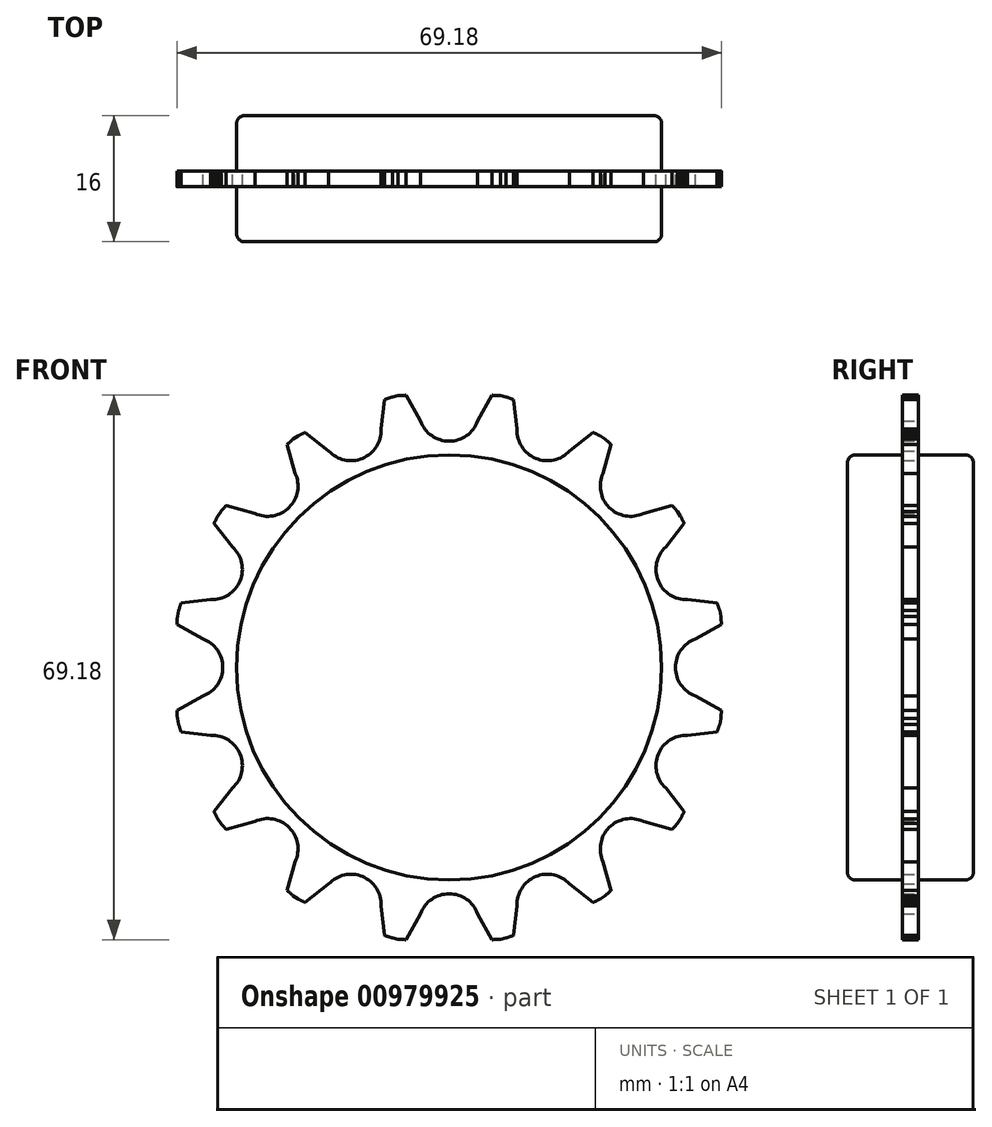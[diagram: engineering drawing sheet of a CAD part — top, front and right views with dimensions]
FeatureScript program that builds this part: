
annotation { "Feature Type Name" : "Feature", "Feature Type Description" : "" }
export const myFeature = defineFeature(function(context is Context, id is Id, definition is map)
    precondition{}
    {
        {
            var Q0;
            Q0=qCreatedBy(makeId("Front.planeOp"),FACE);
            var sketch = newSketch(context, id + "F0", { "sketchPlane" : qUnion([Q0])});
            skArc(sketch, "E0", {"start": v(-3.62, 31.28) * mm, "mid": v(0, 28.75) * mm, "end": v(3.62, 31.28) * mm});
            skPoint(sketch, "E1.center", {"position": v(0, -0.09) * mm});
            skArc(sketch, "E2.trimOffspring", {"start": v(6.5, 34.52) * mm, "mid": v(5.98, 34.55) * mm, "end": v(5.47, 34.59) * mm});
            skArc(sketch, "E3.1.5", {"start": v(-5.47, 34.59) * mm, "mid": v(-5.98, 34.55) * mm, "end": v(-6.5, 34.52) * mm});
            skLineSegment(sketch, "E4", {"start": v(3.62, 31.28) * mm, "end": v(5.47, 34.59) * mm});
            skLineSegment(sketch, "E5.MirrorCS", {"start": v(-3.62, 31.28) * mm, "end": v(-5.47, 34.59) * mm});
            skArc(sketch, "E6.1.0", {"start": v(-15.31, 27.51) * mm, "mid": v(-11, 26.56) * mm, "end": v(-8.63, 30.28) * mm});
            skLineSegment(sketch, "E6.1.1", {"start": v(-8.63, 30.28) * mm, "end": v(-8.18, 34.05) * mm});
            skArc(sketch, "E6.1.2", {"start": v(-7.21, 34.37) * mm, "mid": v(-7.7, 34.21) * mm, "end": v(-8.18, 34.05) * mm});
            skArc(sketch, "E6.1.3", {"start": v(-18.3, 29.86) * mm, "mid": v(-18.75, 29.63) * mm, "end": v(-19.2, 29.4) * mm});
            skLineSegment(sketch, "E6.1.4", {"start": v(-15.31, 27.51) * mm, "end": v(-18.3, 29.86) * mm});
            skArc(sketch, "E6.2.0", {"start": v(-24.67, 19.56) * mm, "mid": v(-20.33, 20.33) * mm, "end": v(-19.56, 24.67) * mm});
            skLineSegment(sketch, "E6.2.1", {"start": v(-19.56, 24.67) * mm, "end": v(-20.59, 28.33) * mm});
            skArc(sketch, "E6.2.2", {"start": v(-19.82, 29) * mm, "mid": v(-20.2, 28.66) * mm, "end": v(-20.59, 28.33) * mm});
            skArc(sketch, "E6.2.3", {"start": v(-28.33, 20.59) * mm, "mid": v(-28.66, 20.2) * mm, "end": v(-29, 19.82) * mm});
            skLineSegment(sketch, "E6.2.4", {"start": v(-24.67, 19.56) * mm, "end": v(-28.33, 20.59) * mm});
            skArc(sketch, "E6.3.0", {"start": v(-30.28, 8.63) * mm, "mid": v(-26.56, 11) * mm, "end": v(-27.51, 15.31) * mm});
            skLineSegment(sketch, "E6.3.1", {"start": v(-27.51, 15.31) * mm, "end": v(-29.86, 18.3) * mm});
            skArc(sketch, "E6.3.2", {"start": v(-29.4, 19.2) * mm, "mid": v(-29.63, 18.75) * mm, "end": v(-29.86, 18.3) * mm});
            skArc(sketch, "E6.3.3", {"start": v(-34.05, 8.18) * mm, "mid": v(-34.21, 7.7) * mm, "end": v(-34.37, 7.21) * mm});
            skLineSegment(sketch, "E6.3.4", {"start": v(-30.28, 8.63) * mm, "end": v(-34.05, 8.18) * mm});
            skArc(sketch, "E6.4.0", {"start": v(-31.28, -3.62) * mm, "mid": v(-28.75, 0) * mm, "end": v(-31.28, 3.62) * mm});
            skLineSegment(sketch, "E6.4.1", {"start": v(-31.28, 3.62) * mm, "end": v(-34.59, 5.47) * mm});
            skArc(sketch, "E6.4.2", {"start": v(-34.52, 6.5) * mm, "mid": v(-34.55, 5.98) * mm, "end": v(-34.59, 5.47) * mm});
            skArc(sketch, "E6.4.3", {"start": v(-34.59, -5.47) * mm, "mid": v(-34.55, -5.98) * mm, "end": v(-34.52, -6.5) * mm});
            skLineSegment(sketch, "E6.4.4", {"start": v(-31.28, -3.62) * mm, "end": v(-34.59, -5.47) * mm});
            skArc(sketch, "E6.5.0", {"start": v(-27.51, -15.31) * mm, "mid": v(-26.56, -11) * mm, "end": v(-30.28, -8.63) * mm});
            skLineSegment(sketch, "E6.5.1", {"start": v(-30.28, -8.63) * mm, "end": v(-34.05, -8.18) * mm});
            skArc(sketch, "E6.5.2", {"start": v(-34.37, -7.21) * mm, "mid": v(-34.21, -7.7) * mm, "end": v(-34.05, -8.18) * mm});
            skArc(sketch, "E6.5.3", {"start": v(-29.86, -18.3) * mm, "mid": v(-29.63, -18.75) * mm, "end": v(-29.4, -19.2) * mm});
            skLineSegment(sketch, "E6.5.4", {"start": v(-27.51, -15.31) * mm, "end": v(-29.86, -18.3) * mm});
            skArc(sketch, "E6.6.0", {"start": v(-19.56, -24.67) * mm, "mid": v(-20.33, -20.33) * mm, "end": v(-24.67, -19.56) * mm});
            skLineSegment(sketch, "E6.6.1", {"start": v(-24.67, -19.56) * mm, "end": v(-28.33, -20.59) * mm});
            skArc(sketch, "E6.6.2", {"start": v(-29, -19.82) * mm, "mid": v(-28.66, -20.2) * mm, "end": v(-28.33, -20.59) * mm});
            skArc(sketch, "E6.6.3", {"start": v(-20.59, -28.33) * mm, "mid": v(-20.2, -28.66) * mm, "end": v(-19.82, -29) * mm});
            skLineSegment(sketch, "E6.6.4", {"start": v(-19.56, -24.67) * mm, "end": v(-20.59, -28.33) * mm});
            skArc(sketch, "E6.7.0", {"start": v(-8.63, -30.28) * mm, "mid": v(-11, -26.56) * mm, "end": v(-15.31, -27.51) * mm});
            skLineSegment(sketch, "E6.7.1", {"start": v(-15.31, -27.51) * mm, "end": v(-18.3, -29.86) * mm});
            skArc(sketch, "E6.7.2", {"start": v(-19.2, -29.4) * mm, "mid": v(-18.75, -29.63) * mm, "end": v(-18.3, -29.86) * mm});
            skArc(sketch, "E6.7.3", {"start": v(-8.18, -34.05) * mm, "mid": v(-7.7, -34.21) * mm, "end": v(-7.21, -34.37) * mm});
            skLineSegment(sketch, "E6.7.4", {"start": v(-8.63, -30.28) * mm, "end": v(-8.18, -34.05) * mm});
            skArc(sketch, "E6.8.0", {"start": v(3.62, -31.28) * mm, "mid": v(0, -28.75) * mm, "end": v(-3.62, -31.28) * mm});
            skLineSegment(sketch, "E6.8.1", {"start": v(-3.62, -31.28) * mm, "end": v(-5.47, -34.59) * mm});
            skArc(sketch, "E6.8.2", {"start": v(-6.5, -34.52) * mm, "mid": v(-5.98, -34.55) * mm, "end": v(-5.47, -34.59) * mm});
            skArc(sketch, "E6.8.3", {"start": v(5.47, -34.59) * mm, "mid": v(5.98, -34.55) * mm, "end": v(6.5, -34.52) * mm});
            skLineSegment(sketch, "E6.8.4", {"start": v(3.62, -31.28) * mm, "end": v(5.47, -34.59) * mm});
            skArc(sketch, "E6.9.0", {"start": v(15.31, -27.51) * mm, "mid": v(11, -26.56) * mm, "end": v(8.63, -30.28) * mm});
            skLineSegment(sketch, "E6.9.1", {"start": v(8.63, -30.28) * mm, "end": v(8.18, -34.05) * mm});
            skArc(sketch, "E6.9.2", {"start": v(7.21, -34.37) * mm, "mid": v(7.7, -34.21) * mm, "end": v(8.18, -34.05) * mm});
            skArc(sketch, "E6.9.3", {"start": v(18.3, -29.86) * mm, "mid": v(18.75, -29.63) * mm, "end": v(19.2, -29.4) * mm});
            skLineSegment(sketch, "E6.9.4", {"start": v(15.31, -27.51) * mm, "end": v(18.3, -29.86) * mm});
            skArc(sketch, "E6.10.0", {"start": v(24.67, -19.56) * mm, "mid": v(20.33, -20.33) * mm, "end": v(19.56, -24.67) * mm});
            skLineSegment(sketch, "E6.10.1", {"start": v(19.56, -24.67) * mm, "end": v(20.59, -28.33) * mm});
            skArc(sketch, "E6.10.2", {"start": v(19.82, -29) * mm, "mid": v(20.2, -28.66) * mm, "end": v(20.59, -28.33) * mm});
            skArc(sketch, "E6.10.3", {"start": v(28.33, -20.59) * mm, "mid": v(28.66, -20.2) * mm, "end": v(29, -19.82) * mm});
            skLineSegment(sketch, "E6.10.4", {"start": v(24.67, -19.56) * mm, "end": v(28.33, -20.59) * mm});
            skArc(sketch, "E6.11.0", {"start": v(30.28, -8.63) * mm, "mid": v(26.56, -11) * mm, "end": v(27.51, -15.31) * mm});
            skLineSegment(sketch, "E6.11.1", {"start": v(27.51, -15.31) * mm, "end": v(29.86, -18.3) * mm});
            skArc(sketch, "E6.11.2", {"start": v(29.4, -19.2) * mm, "mid": v(29.63, -18.75) * mm, "end": v(29.86, -18.3) * mm});
            skArc(sketch, "E6.11.3", {"start": v(34.05, -8.18) * mm, "mid": v(34.21, -7.7) * mm, "end": v(34.37, -7.21) * mm});
            skLineSegment(sketch, "E6.11.4", {"start": v(30.28, -8.63) * mm, "end": v(34.05, -8.18) * mm});
            skArc(sketch, "E6.12.0", {"start": v(31.28, 3.62) * mm, "mid": v(28.75, 0) * mm, "end": v(31.28, -3.62) * mm});
            skLineSegment(sketch, "E6.12.1", {"start": v(31.28, -3.62) * mm, "end": v(34.59, -5.47) * mm});
            skArc(sketch, "E6.12.2", {"start": v(34.52, -6.5) * mm, "mid": v(34.55, -5.98) * mm, "end": v(34.59, -5.47) * mm});
            skArc(sketch, "E6.12.3", {"start": v(34.59, 5.47) * mm, "mid": v(34.55, 5.98) * mm, "end": v(34.52, 6.5) * mm});
            skLineSegment(sketch, "E6.12.4", {"start": v(31.28, 3.62) * mm, "end": v(34.59, 5.47) * mm});
            skArc(sketch, "E6.13.0", {"start": v(27.51, 15.31) * mm, "mid": v(26.56, 11) * mm, "end": v(30.28, 8.63) * mm});
            skLineSegment(sketch, "E6.13.1", {"start": v(30.28, 8.63) * mm, "end": v(34.05, 8.18) * mm});
            skArc(sketch, "E6.13.2", {"start": v(34.37, 7.21) * mm, "mid": v(34.21, 7.7) * mm, "end": v(34.05, 8.18) * mm});
            skArc(sketch, "E6.13.3", {"start": v(29.86, 18.3) * mm, "mid": v(29.63, 18.75) * mm, "end": v(29.4, 19.2) * mm});
            skLineSegment(sketch, "E6.13.4", {"start": v(27.51, 15.31) * mm, "end": v(29.86, 18.3) * mm});
            skArc(sketch, "E6.14.0", {"start": v(19.56, 24.67) * mm, "mid": v(20.33, 20.33) * mm, "end": v(24.67, 19.56) * mm});
            skLineSegment(sketch, "E6.14.1", {"start": v(24.67, 19.56) * mm, "end": v(28.33, 20.59) * mm});
            skArc(sketch, "E6.14.2", {"start": v(29, 19.82) * mm, "mid": v(28.66, 20.2) * mm, "end": v(28.33, 20.59) * mm});
            skArc(sketch, "E6.14.3", {"start": v(20.59, 28.33) * mm, "mid": v(20.2, 28.66) * mm, "end": v(19.82, 29) * mm});
            skLineSegment(sketch, "E6.14.4", {"start": v(19.56, 24.67) * mm, "end": v(20.59, 28.33) * mm});
            skArc(sketch, "E6.15.0", {"start": v(8.63, 30.28) * mm, "mid": v(11, 26.56) * mm, "end": v(15.31, 27.51) * mm});
            skLineSegment(sketch, "E6.15.1", {"start": v(15.31, 27.51) * mm, "end": v(18.3, 29.86) * mm});
            skArc(sketch, "E6.15.2", {"start": v(19.2, 29.4) * mm, "mid": v(18.75, 29.63) * mm, "end": v(18.3, 29.86) * mm});
            skArc(sketch, "E6.15.3", {"start": v(8.18, 34.05) * mm, "mid": v(7.7, 34.21) * mm, "end": v(7.21, 34.37) * mm});
            skLineSegment(sketch, "E6.15.4", {"start": v(8.63, 30.28) * mm, "end": v(8.18, 34.05) * mm});
            skPoint(sketch, "E6.center", {"position": v(0, 0) * mm});
            skCircle(sketch, "E7", {"center": v(0, 0) * mm, "radius": 27 * mm});
            skLineSegment(sketch, "E8", {"start": v(6.5, 34.52) * mm, "end": v(7.21, 34.37) * mm});
            skLineSegment(sketch, "E9", {"start": v(19.2, 29.4) * mm, "end": v(19.82, 29) * mm});
            skLineSegment(sketch, "E10", {"start": v(29, 19.82) * mm, "end": v(29.4, 19.2) * mm});
            skLineSegment(sketch, "E11", {"start": v(34.37, 7.21) * mm, "end": v(34.52, 6.5) * mm});
            skLineSegment(sketch, "E12", {"start": v(34.52, -6.5) * mm, "end": v(34.37, -7.21) * mm});
            skLineSegment(sketch, "E13", {"start": v(29.4, -19.2) * mm, "end": v(29, -19.82) * mm});
            skLineSegment(sketch, "E14", {"start": v(19.82, -29) * mm, "end": v(19.2, -29.4) * mm});
            skLineSegment(sketch, "E15", {"start": v(7.21, -34.37) * mm, "end": v(6.5, -34.52) * mm});
            skLineSegment(sketch, "E16", {"start": v(-6.5, -34.52) * mm, "end": v(-7.21, -34.37) * mm});
            skLineSegment(sketch, "E17", {"start": v(-19.2, -29.4) * mm, "end": v(-19.82, -29) * mm});
            skLineSegment(sketch, "E18", {"start": v(-29, -19.82) * mm, "end": v(-29.4, -19.2) * mm});
            skLineSegment(sketch, "E19", {"start": v(-34.37, -7.21) * mm, "end": v(-34.52, -6.5) * mm});
            skLineSegment(sketch, "E20", {"start": v(-34.52, 6.5) * mm, "end": v(-34.37, 7.21) * mm});
            skLineSegment(sketch, "E21", {"start": v(-29.4, 19.2) * mm, "end": v(-29, 19.82) * mm});
            skLineSegment(sketch, "E22", {"start": v(-19.82, 29) * mm, "end": v(-19.2, 29.4) * mm});
            skLineSegment(sketch, "E23", {"start": v(-7.21, 34.37) * mm, "end": v(-6.5, 34.52) * mm});
            skSolve(sketch);
        }
        {
            var Q0;
            Q0=makeQuery(id+"F0.imprint","IMPRINT",FACE,{"disambiguationData":[TD([[makeQuery(id+"F0.imprint","IMPRINT",EDGE,{"derivedFrom":sQuery(id+"F0.wireOp",EDGE,"E0")}),-1.0]])]});
            extrude(context, id + "F1", {"entities" : qUnion([Q0]), "depth" : 2 * mm, "symmetric" : true});
        }
        {
            var Q0;
            Q0=makeQuery(id+"F0.imprint","IMPRINT",FACE,{"disambiguationData":[TD([[makeQuery(id+"F0.imprint","IMPRINT",EDGE,{"derivedFrom":sQuery(id+"F0.wireOp",EDGE,"E7")}),1.0]])]});
            extrude(context, id + "F2", {"entities" : qUnion([Q0]), "operationType" : NewBodyOperationType.ADD, "depth" : 16 * mm, "symmetric" : true});
        }
        {
            var Q0;
            Q0=makeQuery(id+"F2.opExtrude","CAP_EDGE",EDGE,{"disambiguationData":[OSD([sQuery(id+"F0.wireOp",EDGE,"E7")])],"isStart":false});
            var Q1;
            Q1=makeQuery(id+"F2.opExtrude","CAP_EDGE",EDGE,{"disambiguationData":[OSD([sQuery(id+"F0.wireOp",EDGE,"E7")])],"isStart":true});
            fillet(context, id + "F3", {"entities" : qUnion([Q0, Q1]), "radius" : 1 * mm, "tangentPropagation" : true, "allowEdgeOverflow" : false});
        }
    });
